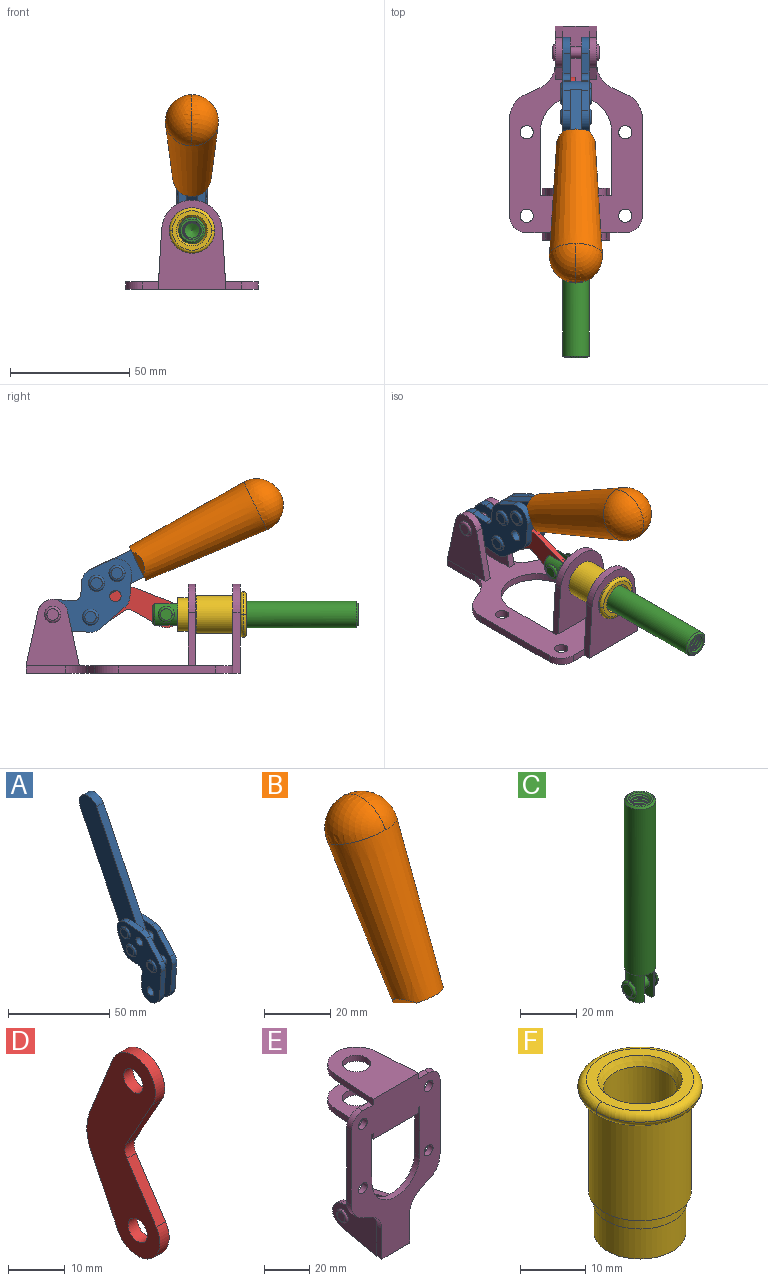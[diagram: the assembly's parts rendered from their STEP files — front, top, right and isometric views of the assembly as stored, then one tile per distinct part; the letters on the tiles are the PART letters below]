
ASSEMBLY  parts=6 mates=6
PART A: 59 faces, bbox 12.9x60.2x99.6 mm
  f0: torus R=2.39mm, axis (-1,0,0), area 14.9mm2, adj f20,f43,f51
  f1: torus R=2.39mm, axis (-1,0,0), area 14.9mm2, adj f19,f42,f51
  f2: torus R=2.39mm, axis (-1,0,0), area 14.9mm2, adj f18,f35,f51
  f3: torus R=2.39mm, axis (-1,0,0), area 14.9mm2, adj f14,f17,f23
  f4: torus R=2.39mm, axis (-1,0,0), area 14.9mm2, adj f13,f16,f23
  f5: torus R=2.39mm, axis (-1,0,0), area 14.9mm2, adj f12,f15,f23
  f6: cylinder r=2.39mm len=4.78mm, axis (1,0,0), area 46.5mm2, adj f48,f50,f51
  f7: cylinder r=2.39mm len=4.78mm, axis (1,0,0), area 46.5mm2, adj f50,f51
  f8: cylinder r=6.35mm len=12.68mm, axis (1,0,0), area 61.8mm2, adj f38,f39,f50,f51
  f9: cylinder r=2.39mm len=4.78mm, axis (-1,0,0), area 70.5mm2, adj f46,f50
  f10: cylinder r=2.39mm len=4.78mm, axis (-1,0,0), area 46.5mm2, adj f23,f45,f46
  f11: cylinder r=2.39mm len=4.78mm, axis (-1,0,0), area 46.5mm2, adj f23,f46
  f12: plane 4.78x4.78mm, normal (1,0,0), area 17.9mm2, adj f5,f15
  f13: plane 4.78x4.78mm, normal (1,0,0), area 17.9mm2, adj f4,f16
  f14: plane 4.78x4.78mm, normal (1,0,0), area 17.9mm2, adj f3,f17
  f15: torus R=2.39mm, axis (-1,0,0), area 14.9mm2, adj f5,f12,f23
  f16: torus R=2.39mm, axis (-1,0,0), area 14.9mm2, adj f4,f13,f23
  f17: torus R=2.39mm, axis (-1,0,0), area 14.9mm2, adj f3,f14,f23
  f18: plane 4.78x4.78mm, normal (-1,0,0), area 17.9mm2, adj f2,f35
  f19: plane 4.78x4.78mm, normal (-1,0,0), area 17.9mm2, adj f1,f42
  f20: plane 4.78x4.78mm, normal (-1,0,0), area 17.9mm2, adj f0,f43
  f21: plane 2.26x0.2mm, normal (1,0,0), area 0.2mm2, adj f31,f44
  f22: plane 2.26x0.2mm, normal (-1,0,0), area 0.2mm2, adj f41,f44
  f23: plane 39.37x30.77mm, normal (1,0,0), area 565.5mm2, adj f3,f4,f5,f10,f11,f15,f16,f17
  f24: cylinder r=6.1mm len=4.15mm, axis (-1,0,0), area 14.7mm2, adj f23,f25,f32,f46
  f25: plane 10.25x9.01mm, normal (0,-0.75,0.66), area 42.3mm2, adj f23,f24,f26,f46
  f26: cylinder r=6.35mm len=4.64mm, axis (-1,0,0), area 15.6mm2, adj f23,f25,f27,f46
  f27: plane 15.84x3.1mm, normal (0,-1,-0.07), area 49.2mm2, adj f23,f26,f28,f46
  f28: cylinder r=6.35mm len=12.68mm, axis (-1,0,0), area 61.8mm2, adj f23,f27,f29,f46
  f29: plane 8.11x3.1mm, normal (0,1,0.07), area 25.2mm2, adj f23,f28,f30,f46
  f30: cylinder r=3.05mm len=3.25mm, axis (-1,0,0), area 14.8mm2, adj f23,f29,f31,f46
  f31: plane 5.99x3.1mm, normal (0,0.07,-1), area 18.6mm2, adj f21,f23,f30,f44,f46
  f32: plane 9.5x3.1mm, normal (0,-0.07,1), area 29.5mm2, adj f23,f24,f33,f46,f47
  f33: cylinder r=6.1mm len=8.63mm, axis (-1,0,0), area 39.1mm2, adj f23,f32,f34,f47
  f34: plane 8.65x3.96mm, normal (0,0.91,-0.42), area 29.5mm2, adj f23,f33,f44,f47
  f35: torus R=2.39mm, axis (-1,0,0), area 14.9mm2, adj f2,f18,f51
  f36: plane 10.25x9.01mm, normal (0,-0.75,0.66), area 42.3mm2, adj f37,f49,f50,f51
  f37: cylinder r=6.35mm len=4.64mm, axis (1,0,0), area 15.6mm2, adj f36,f38,f50,f51
  f38: plane 15.84x3.1mm, normal (0,-1,-0.07), area 49.2mm2, adj f8,f37,f50,f51
  f39: plane 8.11x3.1mm, normal (0,1,0.07), area 25.2mm2, adj f8,f40,f50,f51
  f40: cylinder r=3.05mm len=3.25mm, axis (1,0,0), area 14.8mm2, adj f39,f41,f50,f51
  f41: plane 5.99x3.1mm, normal (0,0.07,-1), area 18.6mm2, adj f22,f40,f44,f50,f51
  f42: torus R=2.39mm, axis (-1,0,0), area 14.9mm2, adj f1,f19,f51
  f43: torus R=2.39mm, axis (-1,0,0), area 14.9mm2, adj f0,f20,f51
  f44: cylinder r=6.35mm len=12.12mm, axis (-1,0,0), area 128.9mm2, adj f21,f22,f23,f31,f34,f41,f46,f47
  f45: plane 2.65x1.35mm, normal (1,0,0), area 1mm2, adj f10,f55
  f46: plane 39.08x20.42mm, normal (-1,0,0), area 412.5mm2, adj f9,f10,f11,f24,f25,f26,f27,f28
  f47: plane 77.62x39.82mm, normal (1,0,0), area 850mm2, adj f32,f33,f34,f44,f53,f54,f55
  f48: plane 2.65x1.35mm, normal (-1,0,0), area 1mm2, adj f6,f55
  f49: cylinder r=6.1mm len=4.15mm, axis (1,0,0), area 14.7mm2, adj f36,f50,f51,f56
  f50: plane 39.08x20.42mm, normal (1,0,0), area 412.5mm2, adj f6,f7,f8,f9,f36,f37,f38,f39
  f51: plane 39.37x30.77mm, normal (-1,0,0), area 565.5mm2, adj f0,f1,f2,f6,f7,f8,f35,f36
  f52: plane 8.65x3.96mm, normal (0,0.91,-0.42), area 29.5mm2, adj f44,f51,f57,f58
  f53: plane 68.49x33.4mm, normal (0,0.9,-0.44), area 358.1mm2, adj f44,f47,f54,f58
  f54: cylinder r=6.35mm len=12.06mm, axis (1,0,0), area 93.7mm2, adj f47,f53,f55,f58
  f55: plane 68.49x33.4mm, normal (0,-0.9,0.44), area 358.1mm2, adj f44,f45,f46,f47,f48,f50,f54,f58
  f56: plane 9.5x3.1mm, normal (0,-0.07,1), area 29.5mm2, adj f49,f50,f51,f57,f58
  f57: cylinder r=6.1mm len=8.63mm, axis (1,0,0), area 39.1mm2, adj f51,f52,f56,f58
  f58: plane 77.62x39.82mm, normal (-1,0,0), area 850mm2, adj f44,f52,f53,f54,f55,f56,f57
PART B: 11 faces, bbox 22.3x42.6x64.5 mm
  f0: sphere r=11.13mm, area 411.4mm2, adj f1,f8
  f1: cone r=11.11mm half-angle=3.3deg, axis (0,0.44,0.9), area 3251.8mm2, adj f0,f7,f8,f9,f10
  f2: cylinder r=6.16mm len=11.7mm, axis (1,0,0), area 89.5mm2, adj f3,f4,f5,f6
  f3: plane 60.23x36.75mm, normal (-1,0,0), area 763.6mm2, adj f2,f4,f6,f10
  f4: plane 51.37x25.05mm, normal (0,0.9,-0.44), area 264.2mm2, adj f2,f3,f5,f10
  f5: plane 60.23x36.75mm, normal (1,0,0), area 763.6mm2, adj f2,f4,f6,f10
  f6: plane 51.37x25.05mm, normal (0,-0.9,0.44), area 264.2mm2, adj f2,f3,f5,f10
  f7: plane 9.95x5.95mm, normal (0.71,-0.31,-0.64), area 25.8mm2, adj f1,f10
  f8: sphere r=11.13mm, area 411.4mm2, adj f0,f1
  f9: plane 9.95x5.95mm, normal (-0.71,-0.31,-0.64), area 25.8mm2, adj f1,f10
  f10: plane 14.27x11.38mm, normal (0,-0.44,-0.9), area 106.7mm2, adj f1,f3,f4,f5,f6,f7,f9
PART C: 48 faces, bbox 12.6x11.1x86.1 mm
  f0: torus R=2.41mm, axis (-1,0,0), area 15mm2, adj f30,f32,f34
  f1: torus R=2.41mm, axis (-1,0,0), area 15mm2, adj f29,f31,f33
  f2: cylinder r=5.54mm len=72.39mm, axis (0,0,1), area 2518.5mm2, adj f3,f4,f42,f43
  f3: cone r=5.54mm half-angle=45deg, axis (0,0,1), area 7.6mm2, adj f2,f5,f41
  f4: cone r=5.54mm half-angle=45deg, axis (0,0,-1), area 34.9mm2, adj f2,f39
  f5: cylinder r=5.08mm len=11.48mm, axis (0,0,1), area 108.3mm2, adj f3,f7,f8,f41
  f6: cylinder r=2.41mm len=4.83mm, axis (-1,0,0), area 71.2mm2, adj f40,f41
  f7: cylinder r=2.41mm len=4.83mm, axis (-1,0,0), area 7.6mm2, adj f5,f34
  f8: cone r=5.08mm half-angle=45deg, axis (0,0,1), area 10.6mm2, adj f5,f37,f41
  f9: cone r=3.98mm half-angle=45deg, axis (0,0,1), area 17.6mm2, adj f27,f39,f45,f46,f47
  f10: cylinder r=2.41mm len=4.83mm, axis (-1,0,0), area 7.6mm2, adj f33,f38
  f11: cylinder r=3.2mm len=6.4mm, axis (0,0,1), area 78.4mm2, adj f12,f28,f44,f45,f47
  f12: cylinder r=3.2mm len=6.4mm, axis (0,0,1), area 10.5mm2, adj f11,f13,f45,f47
  f13: cylinder r=3.2mm len=6.4mm, axis (0,0,1), area 10.5mm2, adj f12,f14,f45,f47
  f14: cylinder r=3.2mm len=6.4mm, axis (0,0,1), area 10.5mm2, adj f13,f15,f45,f47
  f15: cylinder r=3.2mm len=6.4mm, axis (0,0,1), area 10.5mm2, adj f14,f16,f45,f47
  f16: cylinder r=3.2mm len=6.4mm, axis (0,0,1), area 10.5mm2, adj f15,f17,f45,f47
  f17: cylinder r=3.2mm len=6.4mm, axis (0,0,1), area 10.5mm2, adj f16,f18,f45,f47
  f18: cylinder r=3.2mm len=6.4mm, axis (0,0,1), area 10.5mm2, adj f17,f19,f45,f47
  f19: cylinder r=3.2mm len=6.4mm, axis (0,0,1), area 10.5mm2, adj f18,f20,f45,f47
  f20: cylinder r=3.2mm len=6.4mm, axis (0,0,1), area 10.5mm2, adj f19,f21,f45,f47
  f21: cylinder r=3.2mm len=6.4mm, axis (0,0,1), area 10.5mm2, adj f20,f22,f45,f47
  f22: cylinder r=3.2mm len=6.4mm, axis (0,0,1), area 10.5mm2, adj f21,f23,f45,f47
  f23: cylinder r=3.2mm len=6.4mm, axis (0,0,1), area 10.5mm2, adj f22,f24,f45,f47
  f24: cylinder r=3.2mm len=6.4mm, axis (0,0,1), area 10.5mm2, adj f23,f25,f45,f47
  f25: cylinder r=3.2mm len=6.4mm, axis (0,0,1), area 10.5mm2, adj f24,f26,f45,f47
  f26: cylinder r=3.2mm len=6.4mm, axis (0,0,1), area 10.5mm2, adj f25,f27,f45,f47
  f27: cylinder r=3.2mm len=6.4mm, axis (0,0,1), area 7.4mm2, adj f9,f26,f45,f47
  f28: cone r=3.2mm half-angle=60deg, axis (0,0,1), area 37.2mm2, adj f11
  f29: plane 4.83x4.83mm, normal (-1,0,0), area 18.3mm2, adj f1,f31
  f30: plane 4.83x4.83mm, normal (1,0,0), area 18.3mm2, adj f0,f32
  f31: torus R=2.41mm, axis (-1,0,0), area 15mm2, adj f1,f29,f33
  f32: torus R=2.41mm, axis (-1,0,0), area 15mm2, adj f0,f30,f34
  f33: plane 6.83x6.83mm, normal (1,0,0), area 18.3mm2, adj f1,f10,f31
  f34: plane 6.83x6.83mm, normal (-1,0,0), area 18.3mm2, adj f0,f7,f32
  f35: cone r=5.08mm half-angle=45deg, axis (0,0,1), area 10.6mm2, adj f36,f38,f40
  f36: plane 7.25x1.97mm, normal (0,0,-1), area 10mm2, adj f35,f40
  f37: plane 7.25x1.97mm, normal (0,0,-1), area 10mm2, adj f8,f41
  f38: cylinder r=5.08mm len=11.48mm, axis (0,0,1), area 108.3mm2, adj f10,f35,f40,f42
  f39: plane 9.55x9.55mm, normal (0,0,1), area 22mm2, adj f4,f9
  f40: plane 12.76x10.09mm, normal (1,0,0), area 95.7mm2, adj f6,f35,f36,f38,f42,f43
  f41: plane 12.76x10.09mm, normal (-1,0,0), area 95.7mm2, adj f3,f5,f6,f8,f37,f43
  f42: cone r=5.54mm half-angle=45deg, axis (0,0,1), area 7.6mm2, adj f2,f38,f40
  f43: plane 11.07x4.7mm, normal (0,0,-1), area 50.4mm2, adj f2,f40,f41
  f44: plane 0.89x0.62mm, normal (-1,0,0), area 0.3mm2, adj f11,f45,f46,f47
  f45: bspline ~24.8x7.63mm, area 266.6mm2, adj f9,f11,f12,f13,f14,f15,f16,f17
  f46: bspline ~24.87x7.63mm, area 73.6mm2, adj f9,f44,f45,f47
  f47: bspline ~24.98x7.63mm, area 272.5mm2, adj f9,f11,f12,f13,f14,f15,f16,f17
PART D: 12 faces, bbox 2.3x18.2x42.8 mm
  f0: cylinder r=2.4mm len=4.8mm, axis (1,0,0), area 34.9mm2, adj f4,f11
  f1: cylinder r=10.41mm len=8.47mm, axis (1,0,0), area 20.2mm2, adj f4,f9,f10,f11
  f2: cylinder r=3.05mm len=3.16mm, axis (1,0,0), area 7.7mm2, adj f4,f6,f7,f11
  f3: cylinder r=2.4mm len=4.8mm, axis (1,0,0), area 34.9mm2, adj f4,f11
  f4: plane 42.81x18.23mm, normal (-1,0,0), area 414.1mm2, adj f0,f1,f2,f3,f5,f6,f7,f8
  f5: cylinder r=5.54mm len=10.67mm, axis (1,0,0), area 41.8mm2, adj f4,f6,f10,f11
  f6: plane 11.66x6.53mm, normal (0,-0.87,-0.49), area 30.9mm2, adj f2,f4,f5,f11
  f7: plane 11.17x7.33mm, normal (0,-0.84,0.55), area 30.9mm2, adj f2,f4,f8,f11
  f8: cylinder r=5.54mm len=10.51mm, axis (1,0,0), area 41.8mm2, adj f4,f7,f9,f11
  f9: plane 13.67x6.67mm, normal (0,0.9,-0.44), area 35.1mm2, adj f1,f4,f8,f11
  f10: plane 14.1x5.7mm, normal (0,0.93,0.37), area 35.1mm2, adj f1,f4,f5,f11
  f11: plane 42.81x18.23mm, normal (1,0,0), area 414.1mm2, adj f0,f1,f2,f3,f5,f6,f7,f8
PART E: 55 faces, bbox 55.7x37.4x89.8 mm
  f0: torus R=2.41mm, axis (-1,0,0), area 15mm2, adj f11,f15,f25
  f1: torus R=2.41mm, axis (-1,0,0), area 15mm2, adj f10,f12,f22
  f2: cylinder r=2.78mm len=5.56mm, axis (0,-1,0), area 54.2mm2, adj f30,f54
  f3: cylinder r=14.99mm len=29.97mm, axis (0,-1,0), area 145.9mm2, adj f30,f49,f53,f54
  f4: cylinder r=2.78mm len=5.56mm, axis (0,-1,0), area 54.2mm2, adj f30,f54
  f5: cylinder r=2.78mm len=5.56mm, axis (0,-1,0), area 54.2mm2, adj f30,f54
  f6: cylinder r=2.78mm len=5.56mm, axis (0,-1,0), area 54.2mm2, adj f30,f54
  f7: cylinder r=6.35mm len=12.7mm, axis (0,0,1), area 123.6mm2, adj f27,f51
  f8: cylinder r=6.35mm len=12.7mm, axis (0,0,-1), area 124.7mm2, adj f21,f35
  f9: cylinder r=2.41mm len=11.18mm, axis (-1,0,0), area 169.4mm2, adj f16,f19
  f10: plane 4.83x4.83mm, normal (1,0,0), area 18.3mm2, adj f1,f12
  f11: plane 4.83x4.83mm, normal (-1,0,0), area 18.3mm2, adj f0,f15
  f12: torus R=2.41mm, axis (-1,0,0), area 15mm2, adj f1,f10,f22
  f13: cylinder r=6.35mm len=12.41mm, axis (1,0,0), area 53.4mm2, adj f18,f19,f22,f23
  f14: cylinder r=6.35mm len=12.41mm, axis (-1,0,0), area 53.4mm2, adj f16,f17,f24,f25
  f15: torus R=2.41mm, axis (-1,0,0), area 15mm2, adj f0,f11,f25
  f16: plane 27.86x22.35mm, normal (1,0,0), area 425.4mm2, adj f9,f14,f17,f24,f30
  f17: plane 22.86x4.97mm, normal (0,0.21,0.98), area 72.5mm2, adj f14,f16,f25,f30
  f18: plane 22.86x4.97mm, normal (0,0.21,0.98), area 72.5mm2, adj f13,f19,f22,f30
  f19: plane 27.86x22.35mm, normal (-1,0,0), area 425.4mm2, adj f9,f13,f18,f23,f30
  f20: cylinder r=12.7mm len=25.35mm, axis (0,0,-1), area 119.8mm2, adj f21,f34,f35,f36
  f21: plane 34.21x28.07mm, normal (0,0,-1), area 702.4mm2, adj f8,f20,f30,f34,f36
  f22: plane 27.96x22.45mm, normal (1,0,0), area 407.2mm2, adj f1,f12,f13,f18,f23,f30,f42,f43
  f23: plane 22.86x4.97mm, normal (0,0.21,-0.98), area 72.5mm2, adj f13,f19,f22,f44
  f24: plane 22.86x4.97mm, normal (0,0.21,-0.98), area 72.5mm2, adj f14,f16,f25,f44
  f25: plane 27.86x22.35mm, normal (-1,0,0), area 407.1mm2, adj f0,f14,f15,f17,f24,f30,f45,f46
  f26: plane 3.1x0.95mm, normal (0,0,-1), area 2.7mm2, adj f30,f49,f50,f54
  f27: plane 34.21x28.07mm, normal (0,0,1), area 702.4mm2, adj f7,f28,f30,f50,f52
  f28: cylinder r=12.7mm len=25.35mm, axis (0,0,1), area 118.8mm2, adj f27,f50,f51,f52
  f29: plane 3.1x0.95mm, normal (0,0,-1), area 2.7mm2, adj f30,f52,f53,f54
  f30: plane 86.54x55.63mm, normal (0,1,0), area 2362.9mm2, adj f2,f3,f4,f5,f6,f16,f17,f18
  f31: plane 40.56x3.1mm, normal (-1,0,0), area 125.7mm2, adj f30,f32,f48,f54
  f32: cylinder r=7.11mm len=7.11mm, axis (0,-1,0), area 34.6mm2, adj f30,f31,f33,f54
  f33: plane 6.67x3.1mm, normal (0,0,1), area 20.4mm2, adj f30,f32,f34,f54
  f34: plane 25.39x3.13mm, normal (-1,0.06,0), area 79.5mm2, adj f20,f21,f33,f35,f54
  f35: plane 37.31x28.45mm, normal (0,0,1), area 789.9mm2, adj f8,f20,f34,f36,f54
  f36: plane 25.39x3.13mm, normal (1,0.06,0), area 79.5mm2, adj f20,f21,f35,f37,f54
  f37: plane 6.67x3.1mm, normal (0,0,1), area 20.4mm2, adj f30,f36,f38,f54
  f38: cylinder r=7.11mm len=7.11mm, axis (0,-1,0), area 34.6mm2, adj f30,f37,f39,f54
  f39: plane 40.56x3.1mm, normal (1,0,0), area 125.7mm2, adj f30,f38,f40,f54
  f40: cylinder r=11.18mm len=10.16mm, axis (0,-1,0), area 39.5mm2, adj f30,f39,f41,f54
  f41: plane 6.09x3.1mm, normal (0.42,0,-0.91), area 20.8mm2, adj f30,f40,f42,f54
  f42: cylinder r=11.18mm len=9.41mm, axis (0,-1,0), area 37.2mm2, adj f22,f30,f41,f43,f54
  f43: plane 16.5x3.1mm, normal (1,0,0), area 51.1mm2, adj f22,f42,f44,f54
  f44: plane 17.37x3.1mm, normal (0,0,-1), area 53.8mm2, adj f23,f24,f30,f43,f45,f54
  f45: plane 16.5x3.1mm, normal (-1,0,0), area 51.1mm2, adj f25,f44,f46,f54
  f46: cylinder r=11.18mm len=9.41mm, axis (0,-1,0), area 37.2mm2, adj f25,f30,f45,f47,f54
  f47: plane 6.09x3.1mm, normal (-0.42,0,-0.91), area 20.8mm2, adj f30,f46,f48,f54
  f48: cylinder r=11.18mm len=10.16mm, axis (0,-1,0), area 39.5mm2, adj f30,f31,f47,f54
  f49: plane 26.54x3.1mm, normal (-1,0,0), area 82.3mm2, adj f3,f26,f30,f54
  f50: plane 25.39x3.1mm, normal (1,0.06,0), area 78.8mm2, adj f26,f27,f28,f51,f54
  f51: plane 37.31x28.45mm, normal (0,0,-1), area 789.9mm2, adj f7,f28,f50,f52,f54
  f52: plane 25.39x3.1mm, normal (-1,0.06,0), area 78.8mm2, adj f27,f28,f29,f51,f54
  f53: plane 26.54x3.1mm, normal (1,0,0), area 82.3mm2, adj f3,f29,f30,f54
  f54: plane 89.66x55.63mm, normal (0,-1,0), area 2678.5mm2, adj f2,f3,f4,f5,f6,f26,f29,f31
PART F: 15 faces, bbox 20.6x20.6x28.7 mm
  f0: torus R=8.26mm, axis (0,0,1), area 56.8mm2, adj f1,f10,f12
  f1: torus R=8.26mm, axis (0,0,1), area 56.8mm2, adj f0,f6,f13
  f2: cylinder r=5.59mm len=25.91mm, axis (0,0,1), area 909.6mm2, adj f3,f4
  f3: cone r=6.86mm half-angle=45deg, axis (0,0,-1), area 70.2mm2, adj f2,f14
  f4: cone r=6.47mm half-angle=30deg, axis (0,0,1), area 66.7mm2, adj f2,f13
  f5: cylinder r=7.04mm len=14.07mm, axis (0,0,1), area 252.6mm2, adj f11,f14
  f6: torus R=8.26mm, axis (0,0,1), area 56.8mm2, adj f1,f12,f13
  f7: cylinder r=7.16mm len=14.33mm, axis (0,0,1), area 91.5mm2, adj f9,f11
  f8: cylinder r=7.86mm len=18.42mm, axis (0,0,1), area 909.6mm2, adj f9,f10
  f9: plane 15.72x15.72mm, normal (0,0,-1), area 33mm2, adj f7,f8
  f10: plane 16.51x16.51mm, normal (0,0,-1), area 19.9mm2, adj f0,f8,f12
  f11: plane 14.33x14.33mm, normal (0,0,-1), area 5.7mm2, adj f5,f7
  f12: torus R=8.26mm, axis (0,0,1), area 56.8mm2, adj f0,f6,f10
  f13: plane 16.51x16.51mm, normal (0,0,1), area 82.7mm2, adj f1,f4,f6
  f14: plane 14.07x14.07mm, normal (0,0,-1), area 7.8mm2, adj f3,f5
PLACE A rot(axis=(1,0,0),90deg) t=(0,9.14,0)mm
PLACE B rot(axis=(1,0,0),90deg) t=(-0.04,9.14,0)mm
PLACE C rot(axis=(1,0,0),90deg) t=(0,9.14,0)mm
PLACE D rot(axis=(1,0,0),90deg) t=(-1.16,9.14,0)mm
PLACE E rot(axis=(1,0,0),90deg) t=(0,9.14,0)mm fixed
PLACE F rot(axis=(1,0,0),90deg) t=(0,9.14,0)mm
MATE revolute D.f3 <-> A.f4  axis (1,0,0) through (0,25.4,23.5)mm
MATE fastened B.f2 <-> A.f54  axis (1,0,0) through (-2.35,-45.63,71.04)mm
MATE fastened F.f2 <-> E.f7  axis (0,-1,0) through (0,-37.25,24.61)mm
MATE revolute A.f7 <-> E.f0  axis (-1,0,0) through (0,41.23,24.61)mm
MATE slider C.f2 <-> E.f7  axis (0,-1,0) through (0,-49.64,24.61)mm
MATE revolute D.f5 <-> C.f6  axis (1,0,0) through (0,-6.33,24.61)mm
